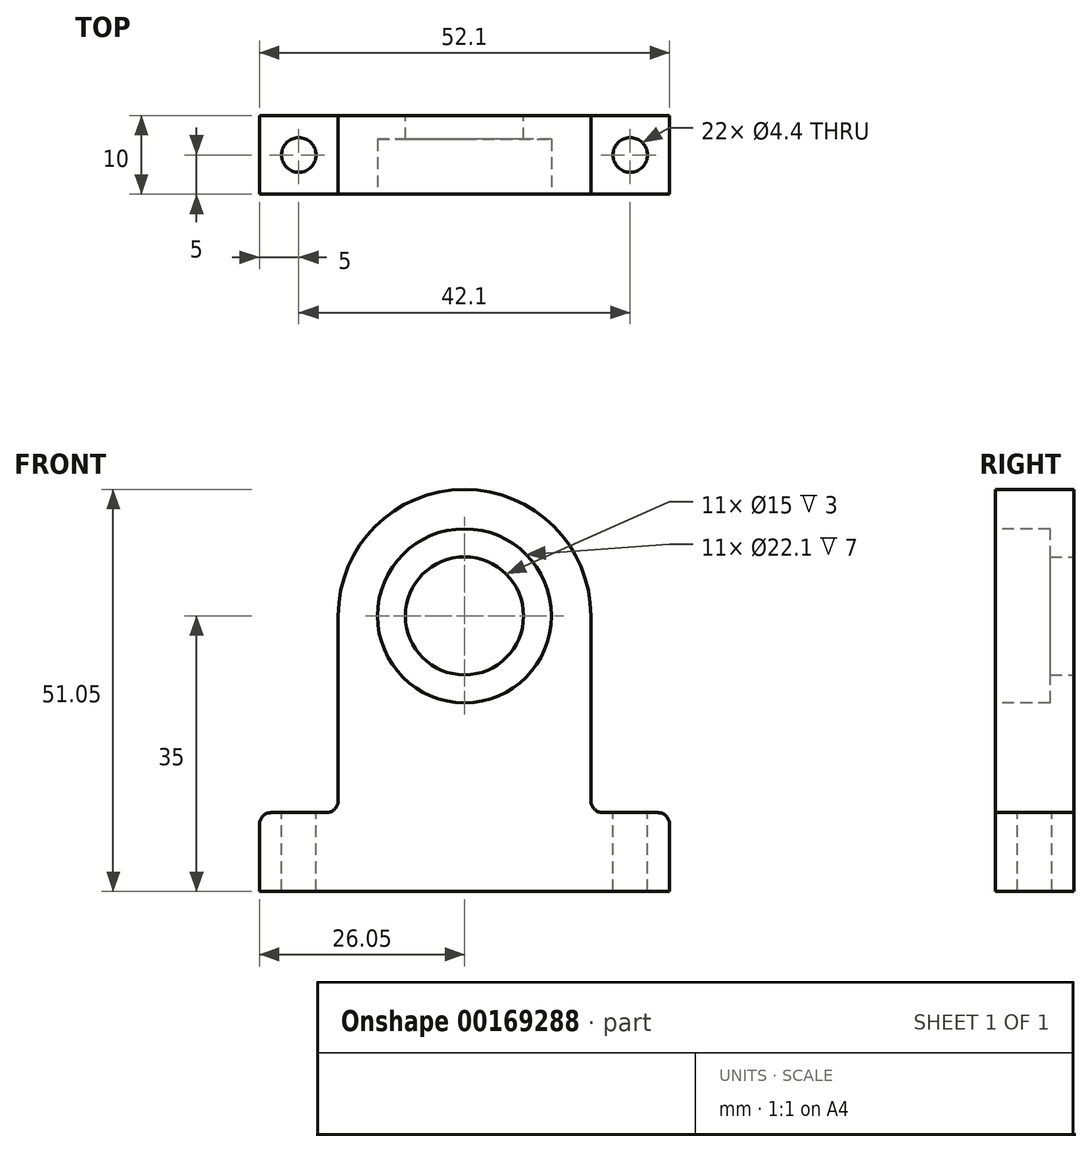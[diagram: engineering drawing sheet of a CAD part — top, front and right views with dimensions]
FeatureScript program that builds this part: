
annotation { "Feature Type Name" : "Feature", "Feature Type Description" : "" }
export const myFeature = defineFeature(function(context is Context, id is Id, definition is map)
    precondition{}
    {
        {
            var Q0;
            Q0=qCreatedBy(makeId("Front.planeOp"),FACE);
            var sketch = newSketch(context, id + "F0", { "sketchPlane" : qUnion([Q0])});
            skLineSegment(sketch, "E0.bottom", {"start": v(-26.05, 27.5) * mm, "end": v(26.05, 27.5) * mm, "construction": true});
            skLineSegment(sketch, "E0.top", {"start": v(-26.05, -27.5) * mm, "end": v(26.05, -27.5) * mm});
            skLineSegment(sketch, "E0.left", {"start": v(-26.05, 27.5) * mm, "end": v(-26.05, -27.5) * mm});
            skLineSegment(sketch, "E0.right", {"start": v(26.05, 27.5) * mm, "end": v(26.05, -27.5) * mm});
            skPoint(sketch, "E0.middle", {"position": v(0, 0) * mm});
            skLineSegment(sketch, "E1", {"start": v(0, -27.5) * mm, "end": v(0, 27.5) * mm, "construction": true});
            skCircle(sketch, "E2", {"center": v(0, 7.5) * mm, "radius": 11.05 * mm});
            skCircle(sketch, "E3", {"center": v(0, 7.5) * mm, "radius": 7.5 * mm});
            skLineSegment(sketch, "E4", {"start": v(-16.05, 27.5) * mm, "end": v(-16.05, -27.5) * mm});
            skArc(sketch, "E5", {"start": v(16.05, 7.5) * mm, "mid": v(0, 23.55) * mm, "end": v(-16.05, 7.5) * mm});
            skLineSegment(sketch, "E6.MirrorCS", {"start": v(16.05, 27.5) * mm, "end": v(16.05, -27.5) * mm});
            skLineSegment(sketch, "E7", {"start": v(-26.05, -17.5) * mm, "end": v(26.05, -17.5) * mm});
            skSolve(sketch);
        }
        {
            var Q0;
            {var subQ0=sQuery(id+"F0.wireOp",EDGE,"E0.left");var subQ1=sQuery(id+"F0.wireOp",EDGE,"E0.top");var subQ2=makeQuery(id+"F0.imprint","INTERSECT",VERTEX,{"derivedFrom":[subQ1,subQ0]});Q0=makeQuery(id+"F0.imprint","IMPRINT",FACE,{"disambiguationData":[TD([[makeQuery(id+"F0.imprint","IMPRINT",EDGE,{"disambiguationData":[TD([[subQ2,-1.0]])],"derivedFrom":subQ1}),1.0]])]});}
            var Q1;
            {var subQ0=sQuery(id+"F0.wireOp",EDGE,"E4");var subQ1=sQuery(id+"F0.wireOp",EDGE,"E0.top");var subQ2=makeQuery(id+"F0.imprint","INTERSECT",VERTEX,{"derivedFrom":[subQ1,subQ0]});Q1=makeQuery(id+"F0.imprint","IMPRINT",FACE,{"disambiguationData":[TD([[makeQuery(id+"F0.imprint","IMPRINT",EDGE,{"disambiguationData":[TD([[subQ2,-1.0]])],"derivedFrom":subQ1}),1.0]])]});}
            var Q2;
            {var subQ0=sQuery(id+"F0.wireOp",EDGE,"E0.right");var subQ1=sQuery(id+"F0.wireOp",EDGE,"E0.top");var subQ2=makeQuery(id+"F0.imprint","INTERSECT",VERTEX,{"derivedFrom":[subQ1,subQ0]});Q2=makeQuery(id+"F0.imprint","IMPRINT",FACE,{"disambiguationData":[TD([[makeQuery(id+"F0.imprint","IMPRINT",EDGE,{"disambiguationData":[TD([[subQ2,1.0]])],"derivedFrom":subQ1}),1.0]])]});}
            var Q3;
            Q3=makeQuery(id+"F0.imprint","IMPRINT",FACE,{"disambiguationData":[TD([[makeQuery(id+"F0.imprint","IMPRINT",EDGE,{"derivedFrom":sQuery(id+"F0.wireOp",EDGE,"E2")}),-1.0]])]});
            var Q4;
            Q4=makeQuery(id+"F0.imprint","IMPRINT",FACE,{"disambiguationData":[TD([[makeQuery(id+"F0.imprint","IMPRINT",EDGE,{"derivedFrom":sQuery(id+"F0.wireOp",EDGE,"E2")}),1.0]])]});
            extrude(context, id + "F1", {"entities" : qUnion([Q0, Q1, Q2, Q3, Q4]), "depth" : 10 * mm});
        }
        {
            var Q0;
            Q0=makeQuery(id+"F1.opExtrude","CAP_FACE",FACE,{"disambiguationData":[OSD([sQuery(id+"F0.wireOp",EDGE,"E0.top"),sQuery(id+"F0.wireOp",EDGE,"E0.left"),sQuery(id+"F0.wireOp",EDGE,"E0.right"),sQuery(id+"F0.wireOp",EDGE,"E3"),sQuery(id+"F0.wireOp",EDGE,"E4"),sQuery(id+"F0.wireOp",EDGE,"E5"),sQuery(id+"F0.wireOp",EDGE,"E6.MirrorCS"),sQuery(id+"F0.wireOp",EDGE,"E7")])],"isStart":false});
            var sketch = newSketch(context, id + "F2", { "sketchPlane" : qUnion([Q0])});
            skCircle(sketch, "E8", {"center": v(0, 7.5) * mm, "radius": 11.05 * mm});
            skSolve(sketch);
        }
        {
            var Q0;
            Q0=makeQuery(id+"F2.imprint","IMPRINT",FACE,{"disambiguationData":[TD([[makeQuery(id+"F2.imprint","IMPRINT",EDGE,{"derivedFrom":sQuery(id+"F2.wireOp",EDGE,"E8")}),1.0]])]});
            extrude(context, id + "F3", {"entities" : qUnion([Q0]), "operationType" : NewBodyOperationType.REMOVE, "oppositeDirection" : true, "depth" : 7 * mm});
        }
        {
            var Q0;
            {var subQ0=sQuery(id+"F0.wireOp",EDGE,"E7");Q0=makeQuery(id+"F1.opExtrude","SWEPT_FACE",FACE,{"disambiguationData":[OSD([subQ0]),TDD([makeQuery(id+"F0.imprint","IMPRINT",EDGE,{"disambiguationData":[TD([[makeQuery(id+"F0.imprint","INTERSECT",VERTEX,{"derivedFrom":[sQuery(id+"F0.wireOp",EDGE,"E0.left"),subQ0]}),-1.0]])],"derivedFrom":subQ0})])]});}
            var sketch = newSketch(context, id + "F4", { "sketchPlane" : qUnion([Q0])});
            skPoint(sketch, "E9", {"position": v(-21.05, -5) * mm});
            skPoint(sketch, "E10", {"position": v(21.05, -5) * mm});
            skSolve(sketch);
        }
        {
            var Q0;
            Q0=sQuery(id+"F4.wireOp",VERTEX,"E9");
            var Q1;
            Q1=sQuery(id+"F4.wireOp",VERTEX,"E10");
            var Q2;
            Q2=makeQuery(id+"F1.opExtrude","SWEPT_BODY",BODY,{"disambiguationData":[OSD([sQuery(id+"F0.wireOp",EDGE,"E0.top"),sQuery(id+"F0.wireOp",EDGE,"E0.left"),sQuery(id+"F0.wireOp",EDGE,"E0.right"),sQuery(id+"F0.wireOp",EDGE,"E3"),sQuery(id+"F0.wireOp",EDGE,"E4"),sQuery(id+"F0.wireOp",EDGE,"E5"),sQuery(id+"F0.wireOp",EDGE,"E6.MirrorCS"),sQuery(id+"F0.wireOp",EDGE,"E7")])]});
            hole(context, id + "F5", {"style" : HoleStyle.SIMPLE, "endStyle" : HoleEndStyle.THROUGH, "standardTappedOrClearance" : lookupTablePath({ "standard" : "ISO", "fit" : "Normal", "size" : "M4", "type" : "Clearance" }), "standardBlindInLast" : lookupTablePath({ "fit" : "Standard", "standard" : "ISO", "size" : "M4", "type" : "Clearance" }), "holeDiameter" : 4.4 * mm, "locations" : qUnion([Q0, Q1]), "scope" : qUnion([Q2]), "isTappedThrough" : true});
        }
        {
            var Q0;
            Q0=makeQuery(id+"F1.opExtrude","SWEPT_EDGE",EDGE,{"disambiguationData":[OSD([sQuery(id+"F0.wireOp",EDGE,"E4"),sQuery(id+"F0.wireOp",EDGE,"E7")])]});
            var Q1;
            Q1=makeQuery(id+"F1.opExtrude","SWEPT_EDGE",EDGE,{"disambiguationData":[OSD([sQuery(id+"F0.wireOp",EDGE,"E0.left"),sQuery(id+"F0.wireOp",EDGE,"E7")])]});
            var Q2;
            Q2=makeQuery(id+"F1.opExtrude","SWEPT_EDGE",EDGE,{"disambiguationData":[OSD([sQuery(id+"F0.wireOp",EDGE,"E6.MirrorCS"),sQuery(id+"F0.wireOp",EDGE,"E7")])]});
            var Q3;
            Q3=makeQuery(id+"F1.opExtrude","SWEPT_EDGE",EDGE,{"disambiguationData":[OSD([sQuery(id+"F0.wireOp",EDGE,"E0.right"),sQuery(id+"F0.wireOp",EDGE,"E7")])]});
            fillet(context, id + "F6", {"entities" : qUnion([Q0, Q1, Q2, Q3]), "radius" : 1.5 * mm, "tangentPropagation" : true, "allowEdgeOverflow" : false});
        }
    });
